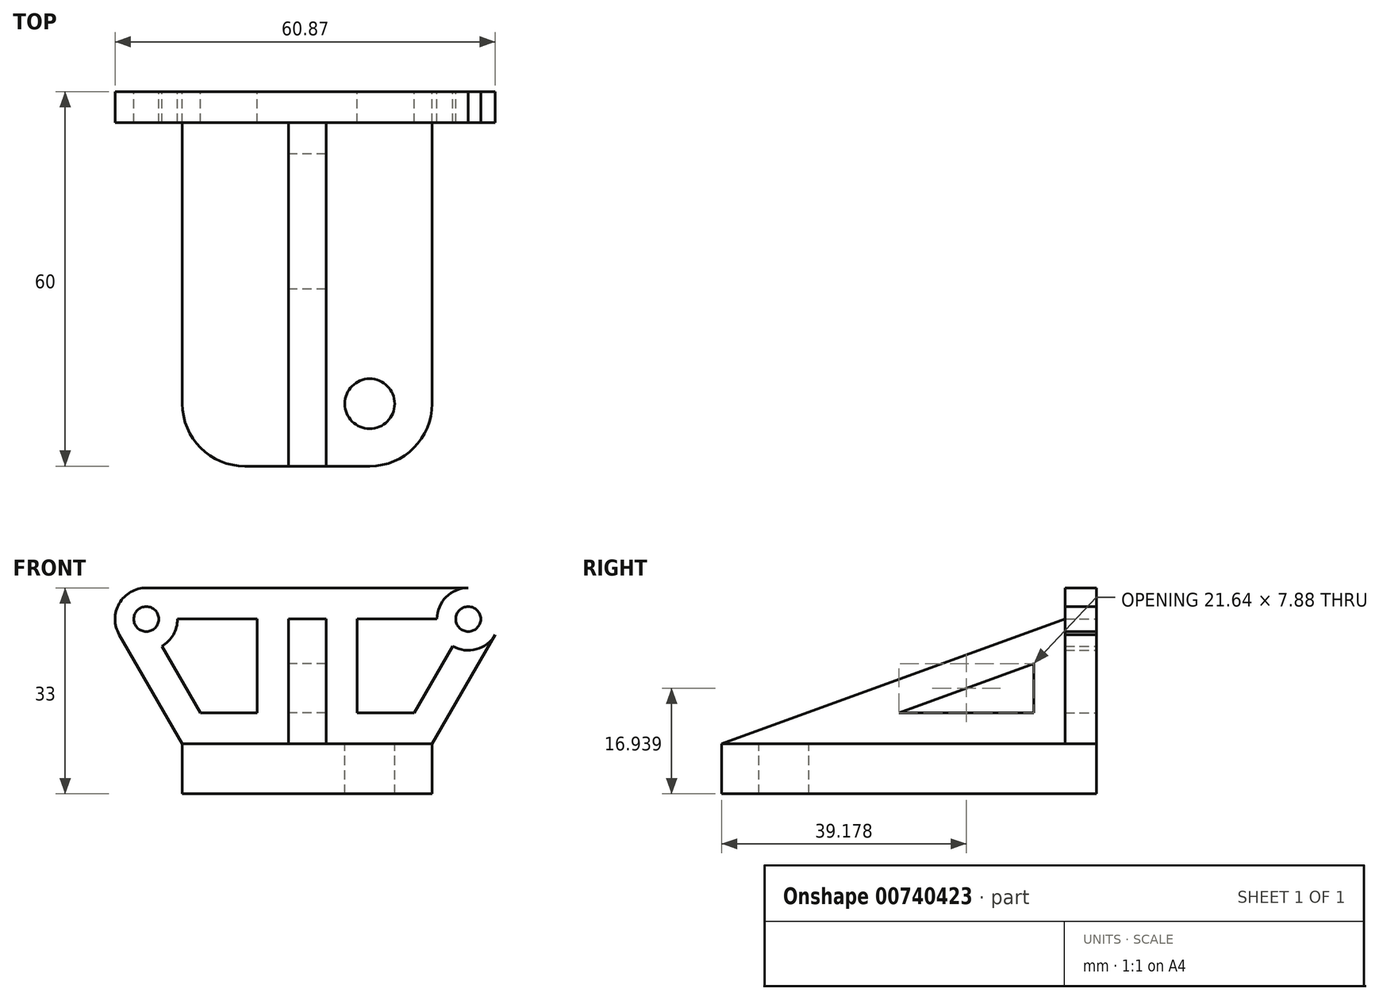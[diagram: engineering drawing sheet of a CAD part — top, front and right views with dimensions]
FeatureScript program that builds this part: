
annotation { "Feature Type Name" : "Feature", "Feature Type Description" : "" }
export const myFeature = defineFeature(function(context is Context, id is Id, definition is map)
    precondition{}
    {
        {
            var Q0;
            Q0=qCreatedBy(makeId("Front.planeOp"),FACE);
            var sketch = newSketch(context, id + "F0", { "sketchPlane" : qUnion([Q0])});
            skLineSegment(sketch, "E0.bottom", {"start": v(0, 0) * mm, "end": v(-20, 0) * mm});
            skLineSegment(sketch, "E0.top", {"start": v(0, -8) * mm, "end": v(-20, -8) * mm});
            skLineSegment(sketch, "E0.left", {"start": v(0, 0) * mm, "end": v(0, -8) * mm});
            skLineSegment(sketch, "E0.right", {"start": v(-20, 0) * mm, "end": v(-20, -8) * mm});
            skLineSegment(sketch, "E1", {"start": v(-20, 0) * mm, "end": v(-30.1, 17.5) * mm});
            skLineSegment(sketch, "E2", {"start": v(0, -8) * mm, "end": v(0, 25) * mm, "construction": true});
            skPoint(sketch, "E2.endSnap0", {"position": v(0, -4) * mm});
            skCircle(sketch, "E3", {"center": v(-25.77, 20) * mm, "radius": 5 * mm});
            skPoint(sketch, "E3.second.point", {"position": v(-20.77, 20) * mm});
            skPoint(sketch, "E3.third.point", {"position": v(-25.77, 25) * mm});
            skCircle(sketch, "E4", {"center": v(-25.77, 20) * mm, "radius": 2 * mm});
            skLineSegment(sketch, "E5", {"start": v(-25.77, 25) * mm, "end": v(0, 25) * mm});
            skLineSegment(sketch, "E6", {"start": v(-23.27, 15.67) * mm, "end": v(-17.11, 5) * mm});
            skLineSegment(sketch, "E7", {"start": v(-20.77, 20) * mm, "end": v(-8, 20) * mm});
            skLineSegment(sketch, "E8", {"start": v(-8, 20) * mm, "end": v(-8, 5) * mm});
            skLineSegment(sketch, "E9", {"start": v(-8, 5) * mm, "end": v(-17.11, 5) * mm});
            skLineSegment(sketch, "E10", {"start": v(-3, 20) * mm, "end": v(-3, 0) * mm});
            skLineSegment(sketch, "E11", {"start": v(-3, 20) * mm, "end": v(0, 20) * mm});
            skLineSegment(sketch, "E12.MirrorCS", {"start": v(25.77, 25) * mm, "end": v(0, 25) * mm});
            skCircle(sketch, "E13.MirrorC", {"center": v(25.77, 20) * mm, "radius": 5 * mm});
            skCircle(sketch, "E14.MirrorC", {"center": v(25.77, 20) * mm, "radius": 2 * mm});
            skLineSegment(sketch, "E15.MirrorCS", {"start": v(20, 0) * mm, "end": v(30.1, 17.5) * mm});
            skLineSegment(sketch, "E16.MirrorCS", {"start": v(23.27, 15.67) * mm, "end": v(17.11, 5) * mm});
            skLineSegment(sketch, "E17.MirrorCS", {"start": v(8, 5) * mm, "end": v(17.11, 5) * mm});
            skLineSegment(sketch, "E18.MirrorCS", {"start": v(8, 20) * mm, "end": v(8, 5) * mm});
            skLineSegment(sketch, "E19.MirrorCS", {"start": v(20.77, 20) * mm, "end": v(8, 20) * mm});
            skLineSegment(sketch, "E20.MirrorCS", {"start": v(3, 20) * mm, "end": v(3, 0) * mm});
            skLineSegment(sketch, "E21.MirrorCS", {"start": v(3, 20) * mm, "end": v(0, 20) * mm});
            skLineSegment(sketch, "E22.MirrorCS", {"start": v(0, -8) * mm, "end": v(20, -8) * mm});
            skLineSegment(sketch, "E23.MirrorCS", {"start": v(0, 0) * mm, "end": v(20, 0) * mm});
            skLineSegment(sketch, "E24.MirrorCS", {"start": v(20, 0) * mm, "end": v(20, -8) * mm});
            skSolve(sketch);
        }
        {
            var Q0;
            {var subQ3=sQuery(id+"F0.wireOp",EDGE,"E1");Q0=makeQuery(id+"F0.imprint","IMPRINT",FACE,{"disambiguationData":[TD([[makeQuery(id+"F0.imprint","IMPRINT",EDGE,{"derivedFrom":subQ3}),-1.0]])]});}
            var Q1;
            Q1=makeQuery(id+"F0.imprint","IMPRINT",FACE,{"disambiguationData":[TD([[makeQuery(id+"F0.imprint","IMPRINT",EDGE,{"derivedFrom":sQuery(id+"F0.wireOp",EDGE,"E4")}),-1.0]])]});
            var Q2;
            Q2=makeQuery(id+"F0.imprint","IMPRINT",FACE,{"disambiguationData":[TD([[makeQuery(id+"F0.imprint","IMPRINT",EDGE,{"derivedFrom":sQuery(id+"F0.wireOp",EDGE,"E14.MirrorC")}),1.0]])]});
            extrude(context, id + "F1", {"entities" : qUnion([Q0, Q1, Q2]), "depth" : 5 * mm});
        }
        {
            var Q0;
            {var subQ1=sQuery(id+"F0.wireOp",EDGE,"E0.left");Q0=makeQuery(id+"F0.imprint","IMPRINT",FACE,{"disambiguationData":[TD([[makeQuery(id+"F0.imprint","IMPRINT",EDGE,{"derivedFrom":subQ1}),1.0]])]});}
            var Q1;
            Q1=makeQuery(id+"F0.imprint","IMPRINT",FACE,{"disambiguationData":[TD([[makeQuery(id+"F0.imprint","IMPRINT",EDGE,{"derivedFrom":sQuery(id+"F0.wireOp",EDGE,"E0.top")}),-1.0]])]});
            extrude(context, id + "F2", {"entities" : qUnion([Q0, Q1]), "depth" : 60 * mm});
        }
        {
            var Q0;
            Q0=qCreatedBy(makeId("Right.planeOp"),FACE);
            var sketch = newSketch(context, id + "F3", { "sketchPlane" : qUnion([Q0])});
            skLineSegment(sketch, "E25", {"start": v(-60, 0) * mm, "end": v(0, 0) * mm});
            skLineSegment(sketch, "E26", {"start": v(0, 0) * mm, "end": v(0, 21.84) * mm});
            skLineSegment(sketch, "E27", {"start": v(0, 21.84) * mm, "end": v(-60, 0) * mm});
            skLineSegment(sketch, "E28.0", {"start": v(-10, 12.88) * mm, "end": v(-31.64, 5) * mm});
            skLineSegment(sketch, "E28.1", {"start": v(-10, 5) * mm, "end": v(-10, 12.88) * mm});
            skLineSegment(sketch, "E28.2", {"start": v(-31.64, 5) * mm, "end": v(-10, 5) * mm});
            skSolve(sketch);
        }
        {
            var Q0;
            Q0=qSketchRegion(id+"F3",true);
            extrude(context, id + "F4", {"entities" : qUnion([Q0]), "operationType" : NewBodyOperationType.ADD, "endBound" : BoundingType.SYMMETRIC, "depth" : 6 * mm});
        }
        {
            var Q0;
            Q0=qCreatedBy(makeId("Top.planeOp"),FACE);
            var sketch = newSketch(context, id + "F5", { "sketchPlane" : qUnion([Q0])});
            skCircle(sketch, "E29", {"center": v(10, -50) * mm, "radius": 4 * mm});
            skCircle(sketch, "E30.MirrorC", {"center": v(-10, -50) * mm, "radius": 4 * mm});
            skSolve(sketch);
        }
        {
            var Q0;
            Q0=makeQuery(id+"F5.imprint","IMPRINT",FACE,{"disambiguationData":[TD([[makeQuery(id+"F5.imprint","IMPRINT",EDGE,{"derivedFrom":sQuery(id+"F5.wireOp",EDGE,"E30.MirrorC")}),-1.0]])]});
            var Q1;
            Q1=makeQuery(id+"F5.imprint","IMPRINT",FACE,{"disambiguationData":[TD([[makeQuery(id+"F5.imprint","IMPRINT",EDGE,{"derivedFrom":sQuery(id+"F5.wireOp",EDGE,"E29")}),1.0]])]});
            extrude(context, id + "F6", {"entities" : qUnion([Q0, Q1]), "operationType" : NewBodyOperationType.REMOVE, "endBound" : BoundingType.THROUGH_ALL, "oppositeDirection" : true, "depth" : 25 * mm});
        }
        {
            var Q0;
            Q0=makeQuery(id+"F2.opExtrude","CAP_EDGE",EDGE,{"disambiguationData":[OSD([sQuery(id+"F0.wireOp",EDGE,"E0.right")])],"isStart":false});
            var Q1;
            Q1=makeQuery(id+"F2.opExtrude","CAP_EDGE",EDGE,{"disambiguationData":[OSD([sQuery(id+"F0.wireOp",EDGE,"E24.MirrorCS")])],"isStart":false});
            fillet(context, id + "F7", {"entities" : qUnion([Q0, Q1]), "radius" : 10 * mm, "tangentPropagation" : true, "allowEdgeOverflow" : false});
        }
    });
